# Revit family: Скамейка чугунная «ВДНХ» Арт 9064
name_source: partatom
category: Антураж
revit_build: Autodesk Revit 2018 (Build: 20180423_1000(x64)
units: mm (PartAtom-declared; Revit-internal decimal feet)

## family parameters
Всегда вертикально = Да
Источник визуального образа = Геометрия семейства
На основе рабочей плоскости = Нет
Общий = Нет
При загрузке вырезать с полостями = Нет
Точка расчета площади = Нет

## types (3) — shared parameters
URL = https://hobbyka.ru
Артикул товара = Арт. 9064
Высота = 970 мм
Группа модели = Скамейки
Изготовитель = ООО «Хоббика»
Изображение типоразмера = Скамейка чугунная «ВДНХ» Арт 9064.jpg
Материал изделия = Сталь, чугун, дерево
Цвет лавки = Дерево
Цвет опоры = Чугун
Ширина = 830 мм

## per-type parameters (varying)
| type | Версия 2,3 м | Версия 3,3 м | Версия 4,3 м | Длина | Описание |
| Версия 2,3 м | Да | Нет | Нет | 2300 мм | Скамейка чугунная «ВДНХ». Версия 2,3 м |
| Версия 3,3 м | Нет | Да | Нет | 3300 мм | Скамейка чугунная «ВДНХ». Версия 3,3 м |
| Версия 4,3 м | Нет | Нет | Да | 4300 мм | Скамейка чугунная «ВДНХ». Версия 4,3 м |
